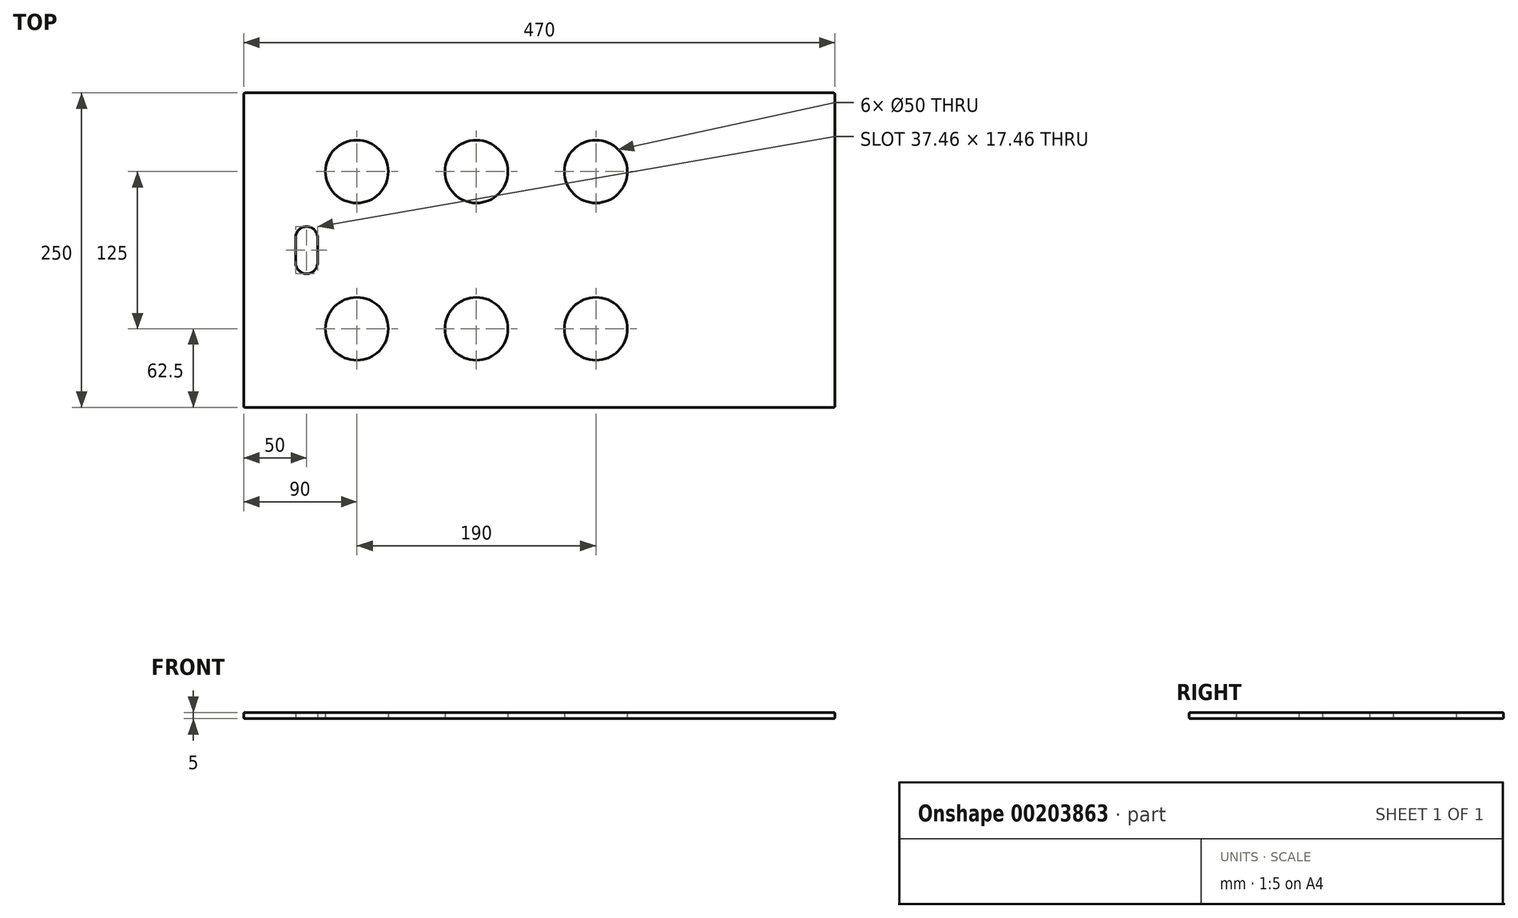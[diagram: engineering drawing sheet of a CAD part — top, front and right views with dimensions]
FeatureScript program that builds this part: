
annotation { "Feature Type Name" : "Feature", "Feature Type Description" : "" }
export const myFeature = defineFeature(function(context is Context, id is Id, definition is map)
    precondition{}
    {
        {
            var Q0;
            Q0=qCreatedBy(makeId("Top.planeOp"),FACE);
            var sketch = newSketch(context, id + "F0", { "sketchPlane" : qUnion([Q0])});
            skLineSegment(sketch, "E0.bottom", {"start": v(235, 125) * mm, "end": v(-235, 125) * mm});
            skLineSegment(sketch, "E0.top", {"start": v(235, -125) * mm, "end": v(-235, -125) * mm});
            skLineSegment(sketch, "E0.left", {"start": v(235, 125) * mm, "end": v(235, -125) * mm});
            skLineSegment(sketch, "E0.right", {"start": v(-235, 125) * mm, "end": v(-235, -125) * mm});
            skPoint(sketch, "E0.middle", {"position": v(0, 0) * mm});
            skPoint(sketch, "E1", {"position": v(-50, 62.5) * mm});
            skLineSegment(sketch, "E2", {"start": v(0, 0) * mm, "end": v(0, 125) * mm, "construction": true});
            skLineSegment(sketch, "E3", {"start": v(-138.05, 0) * mm, "end": v(0, 0) * mm, "construction": true});
            skPoint(sketch, "E4.MirrorP", {"position": v(-145, 62.5) * mm});
            skPoint(sketch, "E5.MirrorP", {"position": v(-145, -62.5) * mm});
            skPoint(sketch, "E6.MirrorP", {"position": v(-50, -62.5) * mm});
            skLineSegment(sketch, "E7", {"start": v(-50, 125) * mm, "end": v(-50, -125) * mm, "construction": true});
            skPoint(sketch, "E8", {"position": v(-50, 0) * mm});
            skLineSegment(sketch, "E9", {"start": v(-158.48, 62.5) * mm, "end": v(127.88, 62.5) * mm, "construction": true});
            skPoint(sketch, "E10.MirrorP", {"position": v(45, 62.5) * mm});
            skPoint(sketch, "E11.MirrorP", {"position": v(45, -62.5) * mm});
            skLineSegment(sketch, "E12", {"start": v(135, 125) * mm, "end": v(135, -125) * mm, "construction": true});
            skLineSegment(sketch, "E13.bottom", {"start": v(-235, -125) * mm, "end": v(-185, -125) * mm, "construction": true});
            skLineSegment(sketch, "E13.top", {"start": v(-235, 0) * mm, "end": v(-185, 0) * mm, "construction": true});
            skLineSegment(sketch, "E13.left", {"start": v(-235, -125) * mm, "end": v(-235, 0) * mm, "construction": true});
            skLineSegment(sketch, "E13.right", {"start": v(-185, -125) * mm, "end": v(-185, 0) * mm, "construction": true});
            skLineSegment(sketch, "E14.left", {"start": v(-176.27, 10) * mm, "end": v(-176.27, -10) * mm});
            skLineSegment(sketch, "E14.right", {"start": v(-193.73, 10) * mm, "end": v(-193.73, -10) * mm});
            skPoint(sketch, "E14.middle", {"position": v(-185, 0) * mm});
            skArc(sketch, "E15", {"start": v(-176.27, 10) * mm, "mid": v(-185, 18.73) * mm, "end": v(-193.73, 10) * mm});
            skArc(sketch, "E16", {"start": v(-193.73, -10) * mm, "mid": v(-185, -18.73) * mm, "end": v(-176.27, -10) * mm});
            skSolve(sketch);
        }
        {
            var Q0;
            Q0=makeQuery(id+"F0.imprint","IMPRINT",FACE,{"disambiguationData":[TD([[makeQuery(id+"F0.imprint","IMPRINT",EDGE,{"derivedFrom":sQuery(id+"F0.wireOp",EDGE,"E0.bottom")}),1.0]])]});
            extrude(context, id + "F1", {"entities" : qUnion([Q0]), "depth" : 5 * mm});
        }
        {
            var Q0;
            Q0=makeQuery(id+"F1.opExtrude","SWEPT_FACE",FACE,{"disambiguationData":[OSD([sQuery(id+"F0.wireOp",EDGE,"E0.top")])]});
            var Q1;
            Q1=makeQuery(id+"F1.opExtrude","SWEPT_FACE",FACE,{"disambiguationData":[OSD([sQuery(id+"F0.wireOp",EDGE,"E0.left")])]});
            var Q2;
            Q2=makeQuery(id+"F1.opExtrude","SWEPT_FACE",FACE,{"disambiguationData":[OSD([sQuery(id+"F0.wireOp",EDGE,"E0.right")])]});
            var Q3;
            Q3=makeQuery(id+"F1.opExtrude","SWEPT_FACE",FACE,{"disambiguationData":[OSD([sQuery(id+"F0.wireOp",EDGE,"E0.bottom")])]});
            fillet(context, id + "F2", {"entities" : qUnion([Q0, Q1, Q2, Q3]), "radius" : 1 * mm, "tangentPropagation" : true, "allowEdgeOverflow" : false});
        }
        {
            var Q0;
            Q0=sQuery(id+"F0.wireOp",VERTEX,"E4.MirrorP");
            var Q1;
            Q1=sQuery(id+"F0.wireOp",VERTEX,"E5.MirrorP");
            var Q2;
            Q2=sQuery(id+"F0.wireOp",VERTEX,"E6.MirrorP");
            var Q3;
            Q3=sQuery(id+"F0.wireOp",VERTEX,"E1");
            var Q4;
            Q4=sQuery(id+"F0.wireOp",VERTEX,"E10.MirrorP");
            var Q5;
            Q5=sQuery(id+"F0.wireOp",VERTEX,"E11.MirrorP");
            var Q6;
            Q6=makeQuery(id+"F1.opExtrude","SWEPT_BODY",BODY,{"disambiguationData":[OSD([sQuery(id+"F0.wireOp",EDGE,"E0.bottom"),sQuery(id+"F0.wireOp",EDGE,"E0.top"),sQuery(id+"F0.wireOp",EDGE,"E0.left"),sQuery(id+"F0.wireOp",EDGE,"E0.right")])]});
            hole(context, id + "F3", {"style" : HoleStyle.SIMPLE, "endStyle" : HoleEndStyle.THROUGH, "oppositeDirection" : true, "holeDiameter" : 50 * mm, "locations" : qUnion([Q0, Q1, Q2, Q3, Q4, Q5]), "scope" : qUnion([Q6]), "isTappedThrough" : true});
        }
    });
